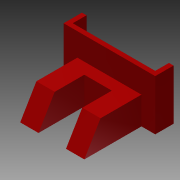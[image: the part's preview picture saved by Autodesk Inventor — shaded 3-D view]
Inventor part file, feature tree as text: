
AUTODESK INVENTOR PART (.ipt)
format: ipt  version: 2013 (Build 170138000, 138)  size: 128,512 bytes
history: native  units: mm
features: extrude x5, sketch x5, other x1
ambient origin geometry x8: Origin, YZ Plane, XZ Plane, XY Plane, X Axis, Y Axis, Z Axis, Center Point
feature tree (11):
  other  "ソリッド1"
  extrude  "押し出し1"  Depth=30.0mm
  extrude  "押し出し4"  Depth=70.0mm TaperAngle=0.0deg
  extrude  "押し出し5"  Depth=67.395mm
  extrude  "押し出し6"  Depth=49.705mm
  extrude  "押し出し7"  Depth=50.0mm
  sketch  "スケッチ1"
  sketch  "スケッチ7"
  sketch  "スケッチ8"
  sketch  "スケッチ9"
  sketch  "スケッチ10"
